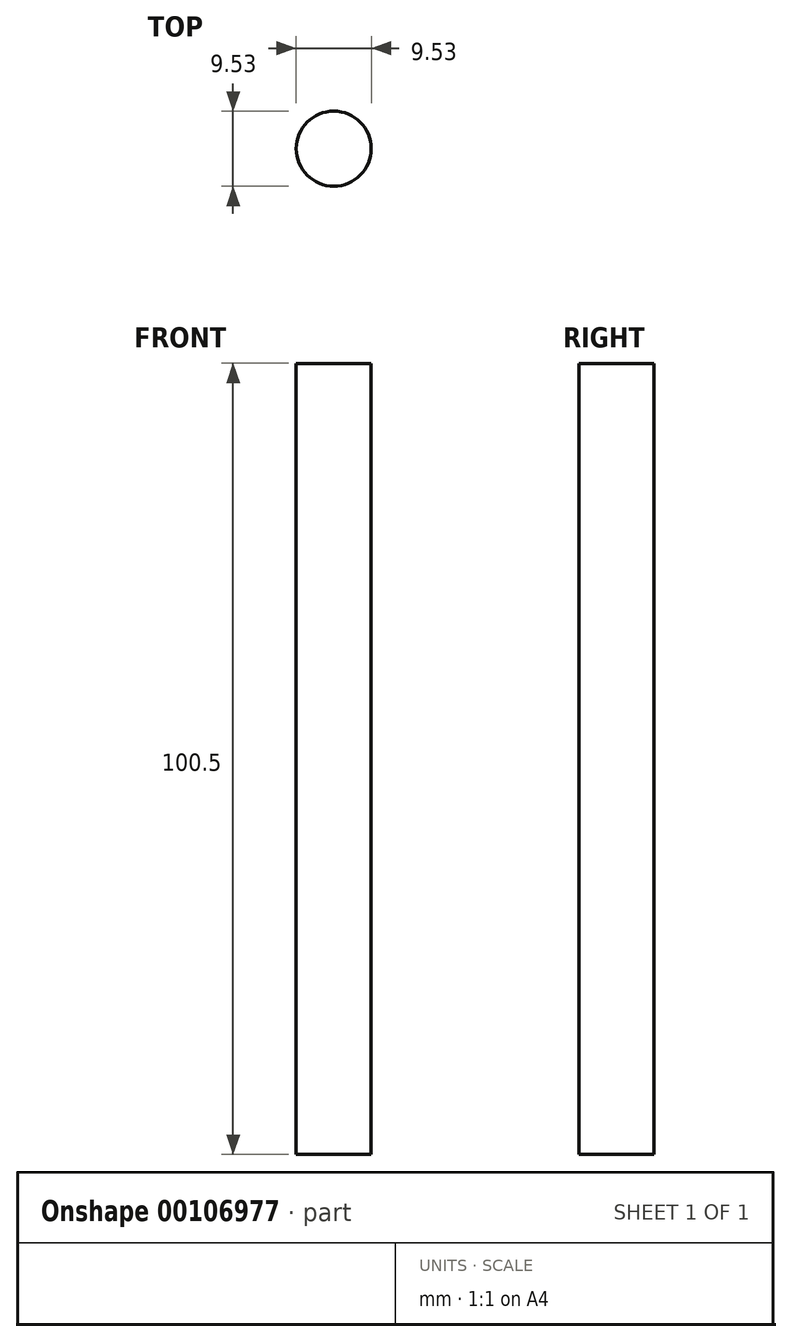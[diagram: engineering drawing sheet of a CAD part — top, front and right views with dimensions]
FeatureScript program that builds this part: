
annotation { "Feature Type Name" : "Feature", "Feature Type Description" : "" }
export const myFeature = defineFeature(function(context is Context, id is Id, definition is map)
    precondition{}
    {
        {
            var Q0;
            Q0=qCreatedBy(makeId("Top.planeOp"),FACE);
            var sketch = newSketch(context, id + "F0", { "sketchPlane" : qUnion([Q0])});
            skCircle(sketch, "E0", {"center": v(-43.1, 5.89) * mm, "radius": 4.76 * mm});
            skSolve(sketch);
        }
        {
            var Q0;
            Q0 = qSketchRegion(id + "F0", true);
            extrude(context, id + "F1", {"entities" : qUnion([Q0]), "depth" : 100.5 * mm});
        }
    });
